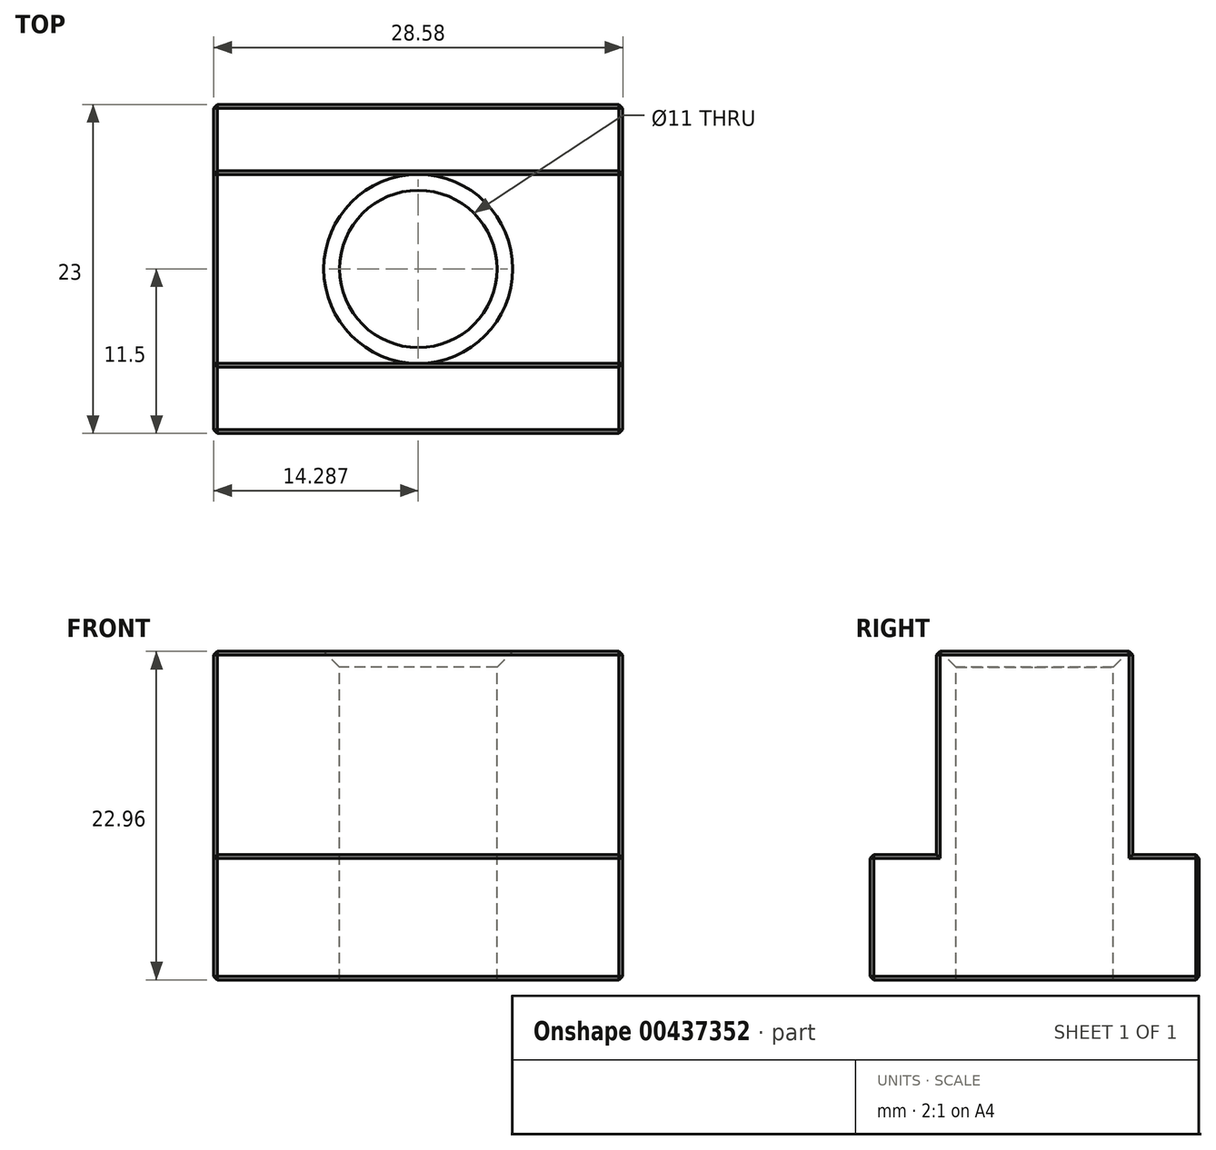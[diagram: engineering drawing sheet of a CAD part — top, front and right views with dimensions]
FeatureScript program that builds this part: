
annotation { "Feature Type Name" : "Feature", "Feature Type Description" : "" }
export const myFeature = defineFeature(function(context is Context, id is Id, definition is map)
    precondition{}
    {
        {
            var Q0;
            Q0=qCreatedBy(makeId("Right.planeOp"),FACE);
            var sketch = newSketch(context, id + "F0", { "sketchPlane" : qUnion([Q0])});
            skLineSegment(sketch, "E0", {"start": v(0, 0) * mm, "end": v(-23, 0) * mm});
            skLineSegment(sketch, "E1", {"start": v(-23, 0) * mm, "end": v(-23, 8.74) * mm});
            skLineSegment(sketch, "E2", {"start": v(-23, 8.74) * mm, "end": v(-18.36, 8.74) * mm});
            skLineSegment(sketch, "E3", {"start": v(-18.36, 8.74) * mm, "end": v(-18.36, 22.96) * mm});
            skLineSegment(sketch, "E4", {"start": v(-18.36, 22.96) * mm, "end": v(-4.64, 22.96) * mm});
            skLineSegment(sketch, "E5", {"start": v(-4.64, 22.96) * mm, "end": v(-4.64, 8.74) * mm});
            skLineSegment(sketch, "E6", {"start": v(-4.64, 8.74) * mm, "end": v(0, 8.74) * mm});
            skLineSegment(sketch, "E7", {"start": v(0, 8.74) * mm, "end": v(0, 0) * mm});
            skPoint(sketch, "E8.positionSnap0", {"position": v(-11.5, 22.96) * mm});
            skPoint(sketch, "E9", {"position": v(-11.5, 0) * mm});
            skSolve(sketch);
        }
        {
            var Q0;
            Q0 = qSketchRegion(id + "F0", true);
            extrude(context, id + "F1", {"entities" : qUnion([Q0]), "depth" : 28.57 * mm});
        }
        {
            var Q0;
            Q0=makeQuery(id+"F1.opExtrude","SWEPT_FACE",FACE,{"disambiguationData":[OSD([sQuery(id+"F0.wireOp",EDGE,"E4")])]});
            var sketch = newSketch(context, id + "F2", { "sketchPlane" : qUnion([Q0])});
            skPoint(sketch, "E10", {"position": v(14.29, -11.5) * mm});
            skPoint(sketch, "E10.positionSnap0", {"position": v(28.58, -11.5) * mm});
            skPoint(sketch, "E11", {"position": v(14.29, -4.64) * mm});
            skSolve(sketch);
        }
        {
            var Q0;
            Q0=sQuery(id+"F2.wireOp",VERTEX,"E10");
            var Q1;
            Q1=makeQuery(id+"F1.opExtrude","SWEPT_BODY",BODY,{"disambiguationData":[OSD([sQuery(id+"F0.wireOp",EDGE,"E0"),sQuery(id+"F0.wireOp",EDGE,"E1"),sQuery(id+"F0.wireOp",EDGE,"E2"),sQuery(id+"F0.wireOp",EDGE,"E3"),sQuery(id+"F0.wireOp",EDGE,"E4"),sQuery(id+"F0.wireOp",EDGE,"E5"),sQuery(id+"F0.wireOp",EDGE,"E6"),sQuery(id+"F0.wireOp",EDGE,"E7")])]});
            hole(context, id + "F3", {"style" : HoleStyle.C_SINK, "endStyle" : HoleEndStyle.THROUGH, "holeDiameter" : 11 * mm, "cSinkDiameter" : 13.2 * mm, "cSinkAngle" : 90 * degree, "isTappedThrough" : true, "tappedDepth" : 12.7 * mm, "tapClearance" : 3, "startFromSketch" : true, "locations" : qUnion([Q0]), "scope" : qUnion([Q1])});
        }
        {
            var Q0;
            Q0=makeQuery(id+"F1.opExtrude","CAP_FACE",FACE,{"disambiguationData":[OSD([sQuery(id+"F0.wireOp",EDGE,"E0"),sQuery(id+"F0.wireOp",EDGE,"E1"),sQuery(id+"F0.wireOp",EDGE,"E2"),sQuery(id+"F0.wireOp",EDGE,"E3"),sQuery(id+"F0.wireOp",EDGE,"E4"),sQuery(id+"F0.wireOp",EDGE,"E5"),sQuery(id+"F0.wireOp",EDGE,"E6"),sQuery(id+"F0.wireOp",EDGE,"E7")])],"isStart":false});
            var Q1;
            Q1=makeQuery(id+"F1.opExtrude","CAP_FACE",FACE,{"disambiguationData":[OSD([sQuery(id+"F0.wireOp",EDGE,"E0"),sQuery(id+"F0.wireOp",EDGE,"E1"),sQuery(id+"F0.wireOp",EDGE,"E2"),sQuery(id+"F0.wireOp",EDGE,"E3"),sQuery(id+"F0.wireOp",EDGE,"E4"),sQuery(id+"F0.wireOp",EDGE,"E5"),sQuery(id+"F0.wireOp",EDGE,"E6"),sQuery(id+"F0.wireOp",EDGE,"E7")])],"isStart":true});
            var Q2;
            Q2=makeQuery(id+"F1.opExtrude","SWEPT_EDGE",EDGE,{"disambiguationData":[OSD([sQuery(id+"F0.wireOp",EDGE,"E3"),sQuery(id+"F0.wireOp",EDGE,"E4")])]});
            var Q3;
            Q3=makeQuery(id+"F1.opExtrude","SWEPT_EDGE",EDGE,{"disambiguationData":[OSD([sQuery(id+"F0.wireOp",EDGE,"E1"),sQuery(id+"F0.wireOp",EDGE,"E2")])]});
            var Q4;
            Q4=makeQuery(id+"F1.opExtrude","SWEPT_EDGE",EDGE,{"disambiguationData":[OSD([sQuery(id+"F0.wireOp",EDGE,"E4"),sQuery(id+"F0.wireOp",EDGE,"E5")])]});
            var Q5;
            Q5=makeQuery(id+"F1.opExtrude","SWEPT_EDGE",EDGE,{"disambiguationData":[OSD([sQuery(id+"F0.wireOp",EDGE,"E0"),sQuery(id+"F0.wireOp",EDGE,"E1")])]});
            var Q6;
            Q6=makeQuery(id+"F1.opExtrude","SWEPT_EDGE",EDGE,{"disambiguationData":[OSD([sQuery(id+"F0.wireOp",EDGE,"E6"),sQuery(id+"F0.wireOp",EDGE,"E7")])]});
            var Q7;
            Q7=makeQuery(id+"F1.opExtrude","SWEPT_EDGE",EDGE,{"disambiguationData":[OSD([sQuery(id+"F0.wireOp",EDGE,"E0"),sQuery(id+"F0.wireOp",EDGE,"E7")])]});
            var Q8;
            Q8=makeQuery(id+"F3.hole-0.boolean.opBoolean","INTERSECT",EDGE,{"derivedFrom":[makeQuery(id+"F1.opExtrude","SWEPT_FACE",FACE,{"disambiguationData":[OSD([sQuery(id+"F0.wireOp",EDGE,"E0")])]}),makeQuery(id+"F3.hole-0.opRevolve","SWEPT_FACE",FACE,{"disambiguationData":[OSD([sQuery(id+"F3.hole-0.sketch.wireOp",EDGE,"core_line_2")])]})]});
            chamfer(context, id + "F4", {"entities" : qUnion([Q0, Q1, Q2, Q3, Q4, Q5, Q6, Q7, Q8]), "width" : 0.25 * mm, "tangentPropagation" : true});
        }
    });
